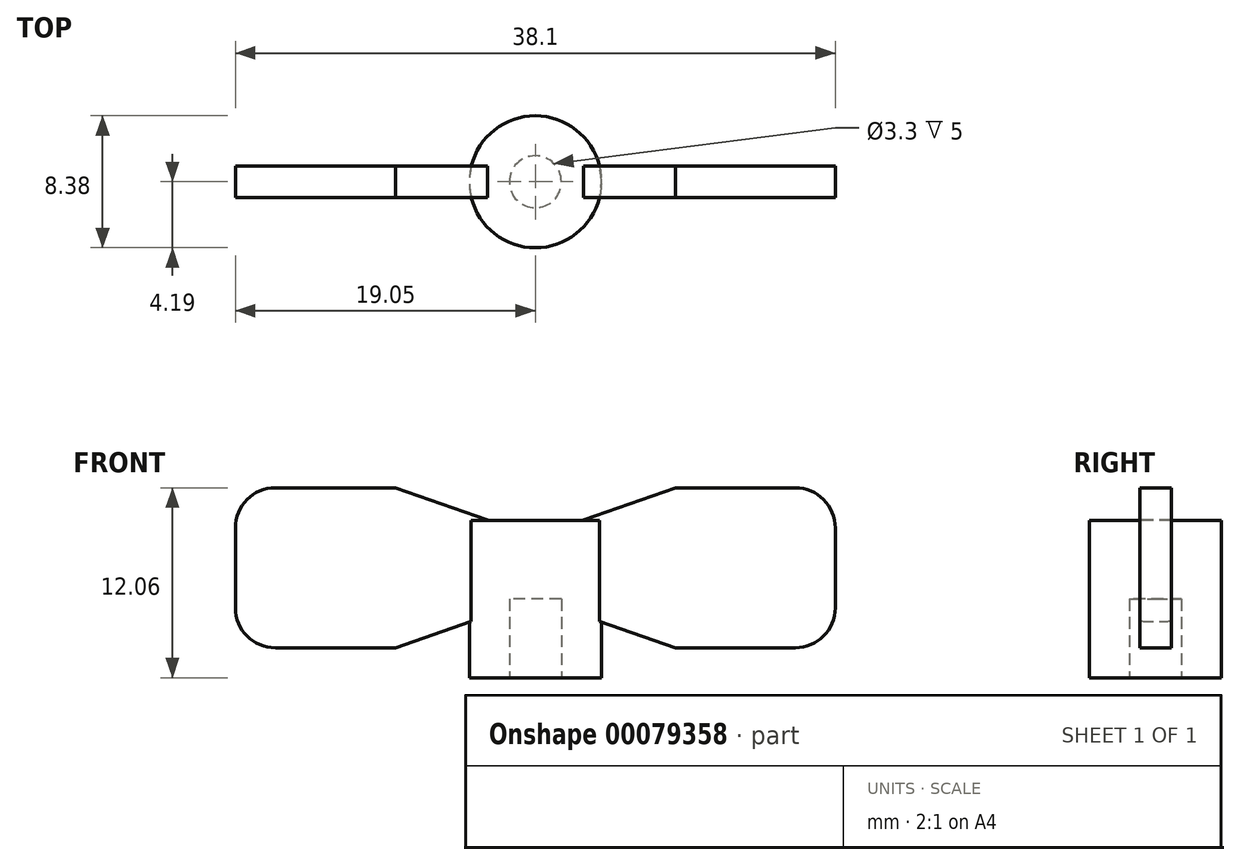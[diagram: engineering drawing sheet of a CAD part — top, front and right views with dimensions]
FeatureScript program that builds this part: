
annotation { "Feature Type Name" : "Feature", "Feature Type Description" : "" }
export const myFeature = defineFeature(function(context is Context, id is Id, definition is map)
    precondition{}
    {
        {
            var Q0;
            Q0=qCreatedBy(makeId("Top.planeOp"),FACE);
            var sketch = newSketch(context, id + "F0", { "sketchPlane" : qUnion([Q0])});
            skCircle(sketch, "E0", {"center": v(0, 0) * mm, "radius": 4.2 * mm});
            skSolve(sketch);
        }
        {
            var Q0;
            Q0 = qSketchRegion(id + "F0", true);
            extrude(context, id + "F1", {"entities" : qUnion([Q0]), "depth" : 10 * mm});
        }
        {
            var Q0;
            Q0=qCreatedBy(makeId("Top.planeOp"),FACE);
            var sketch = newSketch(context, id + "F2", { "sketchPlane" : qUnion([Q0])});
            skCircle(sketch, "E1", {"center": v(0, 0) * mm, "radius": 1.65 * mm});
            skSolve(sketch);
        }
        {
            var Q0;
            Q0 = qSketchRegion(id + "F2", true);
            extrude(context, id + "F3", {"entities" : qUnion([Q0]), "operationType" : NewBodyOperationType.REMOVE, "depth" : 5 * mm});
        }
        {
            var Q0;
            Q0=qCreatedBy(makeId("Front.planeOp"),FACE);
            cPlane(context, id + "F4", {"entities" : qUnion([Q0]), "cplaneType" : CPlaneType.OFFSET, "offset" : 1 * mm, "width" : 152.4 * mm, "height" : 152.4 * mm});
        }
        {
            var Q0;
            Q0=qCreatedBy(id+"F4.planeOp",FACE);
            var sketch = newSketch(context, id + "F5", { "sketchPlane" : qUnion([Q0])});
            skLineSegment(sketch, "E2.bottom", {"start": v(3.05, 3.05) * mm, "end": v(-3.05, 3.05) * mm, "construction": true});
            skLineSegment(sketch, "E2.top", {"start": v(3.05, -3.05) * mm, "end": v(-3.05, -3.05) * mm, "construction": true});
            skLineSegment(sketch, "E2.left", {"start": v(3.05, 3.05) * mm, "end": v(3.05, -3.05) * mm, "construction": true});
            skLineSegment(sketch, "E2.right", {"start": v(-3.05, 3.05) * mm, "end": v(-3.05, -3.05) * mm, "construction": true});
            skPoint(sketch, "E2.middle", {"position": v(0, 0) * mm});
            skLineSegment(sketch, "E3.bottom", {"start": v(16.51, -5.08) * mm, "end": v(8.89, -5.08) * mm, "construction": true});
            skLineSegment(sketch, "E3.top", {"start": v(16.51, 5.08) * mm, "end": v(8.89, 5.08) * mm, "construction": true});
            skLineSegment(sketch, "E3.left", {"start": v(19.05, -2.54) * mm, "end": v(19.05, 2.54) * mm, "construction": true});
            skLineSegment(sketch, "E3.right", {"start": v(8.89, -5.08) * mm, "end": v(8.89, 5.08) * mm});
            skPoint(sketch, "E3.middle", {"position": v(13.97, 0) * mm});
            skLineSegment(sketch, "E4", {"start": v(3.05, -3.05) * mm, "end": v(8.9, -5.08) * mm, "construction": true});
            skLineSegment(sketch, "E5", {"start": v(3.05, 3.05) * mm, "end": v(8.9, 5.08) * mm, "construction": true});
            skLineSegment(sketch, "E6.bottom", {"start": v(-16.51, -5.08) * mm, "end": v(-8.89, -5.08) * mm, "construction": true});
            skLineSegment(sketch, "E6.top", {"start": v(-16.51, 5.08) * mm, "end": v(-8.89, 5.08) * mm, "construction": true});
            skLineSegment(sketch, "E6.left", {"start": v(-19.05, -2.54) * mm, "end": v(-19.05, 2.54) * mm, "construction": true});
            skLineSegment(sketch, "E6.right", {"start": v(-8.89, -5.08) * mm, "end": v(-8.89, 5.08) * mm});
            skPoint(sketch, "E6.middle", {"position": v(-13.97, 0) * mm});
            skLineSegment(sketch, "E7", {"start": v(-3.05, -3.05) * mm, "end": v(-8.89, -5.08) * mm, "construction": true});
            skLineSegment(sketch, "E8", {"start": v(-3.05, 3.05) * mm, "end": v(-8.89, 5.08) * mm, "construction": true});
            skPoint(sketch, "E9.visualSharp", {"position": v(19.05, -5.08) * mm});
            skArc(sketch, "E9.filletArc", {"start": v(16.51, -5.08) * mm, "mid": v(18.3, -4.34) * mm, "end": v(19.05, -2.54) * mm, "construction": true});
            skPoint(sketch, "E10.visualSharp", {"position": v(19.05, 5.08) * mm});
            skArc(sketch, "E10.filletArc", {"start": v(19.05, 2.54) * mm, "mid": v(18.3, 4.34) * mm, "end": v(16.51, 5.08) * mm, "construction": true});
            skPoint(sketch, "E11.visualSharp", {"position": v(-19.05, -5.08) * mm});
            skArc(sketch, "E11.filletArc", {"start": v(-19.05, -2.54) * mm, "mid": v(-18.3, -4.34) * mm, "end": v(-16.51, -5.08) * mm, "construction": true});
            skPoint(sketch, "E12.visualSharp", {"position": v(-19.05, 5.08) * mm});
            skArc(sketch, "E12.filletArc", {"start": v(-16.51, 5.08) * mm, "mid": v(-18.3, 4.34) * mm, "end": v(-19.05, 2.54) * mm, "construction": true});
            skArc(sketch, "E13.0.1.0", {"start": v(16.51, 1.9) * mm, "mid": v(18.3, 2.64) * mm, "end": v(19.05, 4.44) * mm});
            skLineSegment(sketch, "E13.0.1.1", {"start": v(3.05, 10.02) * mm, "end": v(3.05, 3.93) * mm});
            skPoint(sketch, "E13.0.1.2", {"position": v(19.05, 12.06) * mm});
            skLineSegment(sketch, "E13.0.1.3", {"start": v(3.05, 10.02) * mm, "end": v(-3.05, 10.02) * mm});
            skLineSegment(sketch, "E13.0.1.4", {"start": v(3.05, 3.93) * mm, "end": v(-3.05, 3.93) * mm});
            skLineSegment(sketch, "E13.0.1.5", {"start": v(-19.05, 4.44) * mm, "end": v(-19.05, 9.52) * mm});
            skArc(sketch, "E13.0.1.6", {"start": v(-16.51, 12.06) * mm, "mid": v(-18.3, 11.31) * mm, "end": v(-19.05, 9.52) * mm});
            skLineSegment(sketch, "E13.0.1.7", {"start": v(16.51, 12.06) * mm, "end": v(8.89, 12.06) * mm});
            skLineSegment(sketch, "E13.0.1.8", {"start": v(3.05, 10.02) * mm, "end": v(8.9, 12.06) * mm});
            skLineSegment(sketch, "E13.0.1.9", {"start": v(16.51, 1.9) * mm, "end": v(8.89, 1.9) * mm});
            skArc(sketch, "E13.0.1.10", {"start": v(-19.05, 4.44) * mm, "mid": v(-18.3, 2.64) * mm, "end": v(-16.51, 1.9) * mm});
            skPoint(sketch, "E13.0.1.11", {"position": v(13.97, 6.98) * mm});
            skPoint(sketch, "E13.0.1.12", {"position": v(-19.05, 12.06) * mm});
            skLineSegment(sketch, "E13.0.1.13", {"start": v(-16.51, 1.9) * mm, "end": v(-8.89, 1.9) * mm});
            skLineSegment(sketch, "E13.0.1.14", {"start": v(-3.05, 10.02) * mm, "end": v(-8.89, 12.06) * mm});
            skPoint(sketch, "E13.0.1.15", {"position": v(-13.97, 6.98) * mm});
            skLineSegment(sketch, "E13.0.1.16", {"start": v(19.05, 4.44) * mm, "end": v(19.05, 9.52) * mm});
            skPoint(sketch, "E13.0.1.17", {"position": v(0, 6.98) * mm});
            skArc(sketch, "E13.0.1.18", {"start": v(19.05, 9.52) * mm, "mid": v(18.3, 11.31) * mm, "end": v(16.51, 12.06) * mm});
            skLineSegment(sketch, "E13.0.1.19", {"start": v(8.89, 1.9) * mm, "end": v(8.89, 12.06) * mm});
            skPoint(sketch, "E13.0.1.20", {"position": v(19.05, 1.9) * mm});
            skLineSegment(sketch, "E13.0.1.21", {"start": v(3.05, 3.93) * mm, "end": v(8.9, 1.9) * mm});
            skPoint(sketch, "E13.0.1.22", {"position": v(-19.05, 1.9) * mm});
            skLineSegment(sketch, "E13.0.1.23", {"start": v(-3.05, 3.93) * mm, "end": v(-8.89, 1.9) * mm});
            skLineSegment(sketch, "E13.0.1.24", {"start": v(-3.05, 10.02) * mm, "end": v(-3.05, 3.93) * mm});
            skLineSegment(sketch, "E13.0.1.25", {"start": v(-8.89, 1.9) * mm, "end": v(-8.89, 12.06) * mm});
            skLineSegment(sketch, "E13.0.1.26", {"start": v(-16.51, 12.06) * mm, "end": v(-8.89, 12.06) * mm});
            skLineSegment(sketch, "E13.direction1", {"start": v(16.51, -5.08) * mm, "end": v(41.91, -5.08) * mm, "construction": true});
            skLineSegment(sketch, "E13.direction2", {"start": v(16.51, -5.08) * mm, "end": v(16.51, 1.9) * mm, "construction": true});
            skSolve(sketch);
        }
        {
            var Q0;
            Q0=makeQuery(id+"F5.imprint","IMPRINT",FACE,{"disambiguationData":[TD([[makeQuery(id+"F5.imprint","IMPRINT",EDGE,{"derivedFrom":sQuery(id+"F5.wireOp",EDGE,"E13.0.1.5")}),-1.0]])]});
            var Q1;
            {var subQ3=sQuery(id+"F5.wireOp",EDGE,"E13.0.1.14");Q1=makeQuery(id+"F5.imprint","IMPRINT",FACE,{"disambiguationData":[TD([[makeQuery(id+"F5.imprint","IMPRINT",EDGE,{"derivedFrom":subQ3}),1.0]])]});}
            var Q2;
            Q2=makeQuery(id+"F5.imprint","IMPRINT",FACE,{"disambiguationData":[TD([[makeQuery(id+"F5.imprint","IMPRINT",EDGE,{"derivedFrom":sQuery(id+"F5.wireOp",EDGE,"E13.0.1.1")}),1.0]])]});
            var Q3;
            Q3=makeQuery(id+"F5.imprint","IMPRINT",FACE,{"disambiguationData":[TD([[makeQuery(id+"F5.imprint","IMPRINT",EDGE,{"derivedFrom":sQuery(id+"F5.wireOp",EDGE,"E13.0.1.0")}),1.0]])]});
            extrude(context, id + "F6", {"entities" : qUnion([Q0, Q1, Q2, Q3]), "operationType" : NewBodyOperationType.ADD, "oppositeDirection" : true, "depth" : 2 * mm});
        }
    });
